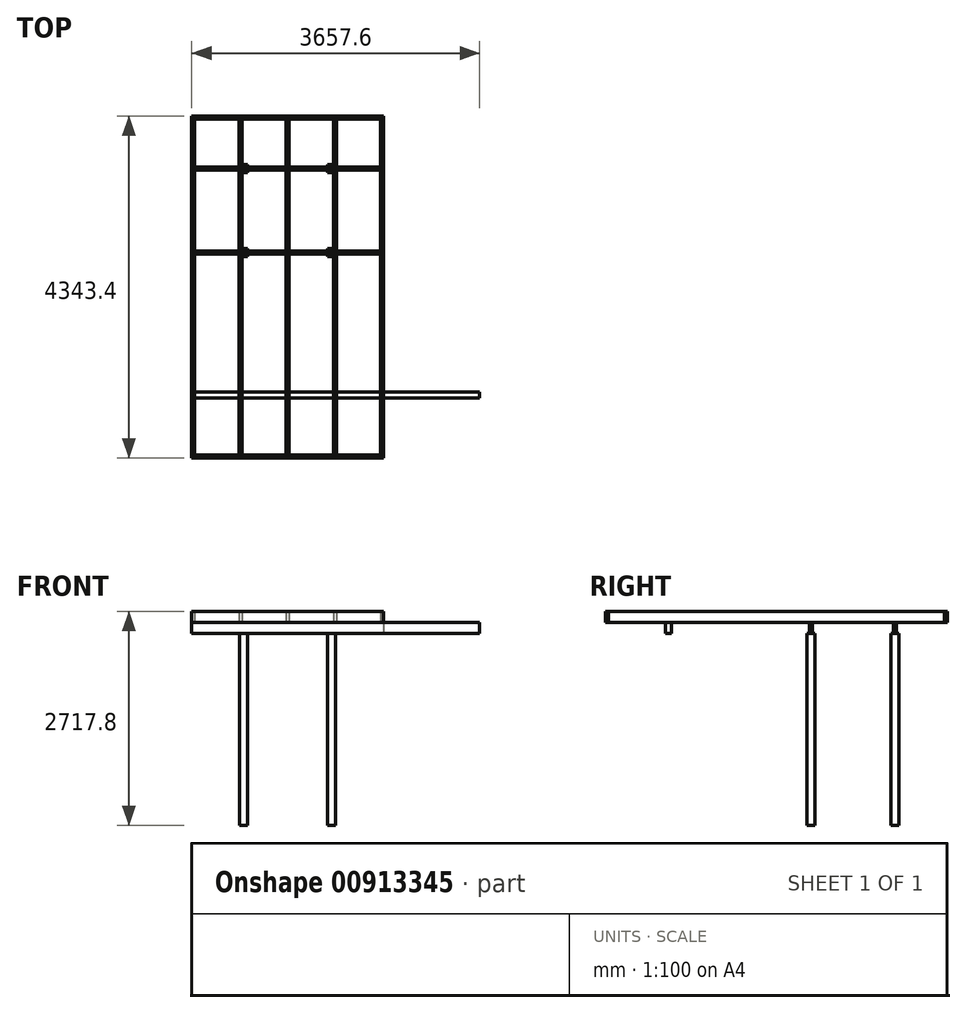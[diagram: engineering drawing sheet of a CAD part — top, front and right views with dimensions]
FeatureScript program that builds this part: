
annotation { "Feature Type Name" : "Feature", "Feature Type Description" : "" }
export const myFeature = defineFeature(function(context is Context, id is Id, definition is map)
    precondition{}
    {
        {
            var Q0;
            Q0=qCreatedBy(makeId("Top.planeOp"),FACE);
            var sketch = newSketch(context, id + "F0", { "sketchPlane" : qUnion([Q0])});
            skLineSegment(sketch, "E0.bottom", {"start": v(-738.08, 153.56) * mm, "end": v(-636.48, 153.56) * mm});
            skLineSegment(sketch, "E0.top", {"start": v(-738.08, 51.96) * mm, "end": v(-636.48, 51.96) * mm});
            skLineSegment(sketch, "E0.left", {"start": v(-738.08, 153.56) * mm, "end": v(-738.08, 51.96) * mm});
            skLineSegment(sketch, "E0.right", {"start": v(-636.48, 153.56) * mm, "end": v(-636.48, 51.96) * mm});
            skLineSegment(sketch, "E1.bottom", {"start": v(379.52, 153.56) * mm, "end": v(481.12, 153.56) * mm});
            skLineSegment(sketch, "E1.top", {"start": v(379.52, 51.96) * mm, "end": v(481.12, 51.96) * mm});
            skLineSegment(sketch, "E1.left", {"start": v(379.52, 153.56) * mm, "end": v(379.52, 51.96) * mm});
            skLineSegment(sketch, "E1.right", {"start": v(481.12, 153.56) * mm, "end": v(481.12, 51.96) * mm});
            skLineSegment(sketch, "E2.direction1", {"start": v(-738.08, 51.96) * mm, "end": v(-712.68, 51.96) * mm, "construction": true});
            skLineSegment(sketch, "E3.bottom", {"start": v(-1347.68, 83.71) * mm, "end": v(1090.72, 83.71) * mm});
            skLineSegment(sketch, "E3.top", {"start": v(-1347.68, 121.81) * mm, "end": v(1090.72, 121.81) * mm});
            skLineSegment(sketch, "E3.left", {"start": v(-1347.68, 83.71) * mm, "end": v(-1347.68, 121.81) * mm});
            skLineSegment(sketch, "E3.right", {"start": v(1090.72, 83.71) * mm, "end": v(1090.72, 121.81) * mm});
            skPoint(sketch, "E4", {"position": v(-738.08, 102.76) * mm});
            skPoint(sketch, "E5", {"position": v(-1347.68, 83.71) * mm});
            skPoint(sketch, "E6", {"position": v(-1347.68, 102.76) * mm});
            skLineSegment(sketch, "E7", {"start": v(-738.08, 102.76) * mm, "end": v(-852.86, 102.76) * mm});
            skLineSegment(sketch, "E8.0.1.0", {"start": v(481.12, -913.24) * mm, "end": v(481.12, -1014.84) * mm});
            skLineSegment(sketch, "E8.0.1.1", {"start": v(379.52, -913.24) * mm, "end": v(379.52, -1014.84) * mm});
            skLineSegment(sketch, "E8.0.1.2", {"start": v(-1347.68, -944.99) * mm, "end": v(1090.72, -944.99) * mm});
            skLineSegment(sketch, "E8.0.1.3", {"start": v(-738.08, -913.24) * mm, "end": v(-636.48, -913.24) * mm});
            skLineSegment(sketch, "E8.0.1.4", {"start": v(-636.48, -913.24) * mm, "end": v(-636.48, -1014.84) * mm});
            skPoint(sketch, "E8.0.1.5", {"position": v(-1347.68, -983.09) * mm});
            skPoint(sketch, "E8.0.1.6", {"position": v(-1347.68, -964.04) * mm});
            skLineSegment(sketch, "E8.0.1.7", {"start": v(379.52, -913.24) * mm, "end": v(481.12, -913.24) * mm});
            skPoint(sketch, "E8.0.1.8", {"position": v(-738.08, -964.04) * mm});
            skLineSegment(sketch, "E8.0.1.9", {"start": v(-738.08, -964.04) * mm, "end": v(-852.86, -964.04) * mm});
            skLineSegment(sketch, "E8.0.1.10", {"start": v(-1347.68, -983.09) * mm, "end": v(1090.72, -983.09) * mm});
            skLineSegment(sketch, "E8.0.1.11", {"start": v(379.52, -1014.84) * mm, "end": v(481.12, -1014.84) * mm});
            skLineSegment(sketch, "E8.0.1.12", {"start": v(-738.08, -1014.84) * mm, "end": v(-636.48, -1014.84) * mm});
            skLineSegment(sketch, "E8.0.1.13", {"start": v(1090.72, -983.09) * mm, "end": v(1090.72, -944.99) * mm});
            skLineSegment(sketch, "E8.0.1.14", {"start": v(-738.08, -913.24) * mm, "end": v(-738.08, -1014.84) * mm});
            skLineSegment(sketch, "E8.0.1.15", {"start": v(-1347.68, -983.09) * mm, "end": v(-1347.68, -944.99) * mm});
            skLineSegment(sketch, "E8.0.1.16", {"start": v(-738.08, -1014.84) * mm, "end": v(-712.68, -1014.84) * mm, "construction": true});
            skLineSegment(sketch, "E8.direction1", {"start": v(-1347.68, 83.71) * mm, "end": v(-1322.28, 83.71) * mm, "construction": true});
            skLineSegment(sketch, "E8.direction2", {"start": v(-1347.68, 83.71) * mm, "end": v(-1347.68, -983.09) * mm, "construction": true});
            skLineSegment(sketch, "E9.bottom", {"start": v(-1347.68, -2811.89) * mm, "end": v(2309.92, -2811.89) * mm});
            skLineSegment(sketch, "E9.top", {"start": v(-1347.68, -2735.69) * mm, "end": v(2309.92, -2735.69) * mm});
            skLineSegment(sketch, "E9.left", {"start": v(-1347.68, -2811.89) * mm, "end": v(-1347.68, -2735.69) * mm});
            skLineSegment(sketch, "E9.right", {"start": v(2309.92, -2811.89) * mm, "end": v(2309.92, -2735.69) * mm});
            skLineSegment(sketch, "E10.bottom", {"start": v(-1347.68, -3421.49) * mm, "end": v(-1309.58, -3421.49) * mm});
            skLineSegment(sketch, "E11.direction1", {"start": v(-1347.68, -3421.49) * mm, "end": v(-747.6, -3421.49) * mm, "construction": true});
            skLineSegment(sketch, "E12.left", {"start": v(-1347.68, -3421.49) * mm, "end": v(-1347.68, -3459.59) * mm});
            skLineSegment(sketch, "E12.right", {"start": v(1090.72, -3421.49) * mm, "end": v(1090.72, -3459.59) * mm});
            skSolve(sketch);
        }
        {
            var Q0;
            {var subQ0=sQuery(id+"F0.wireOp",EDGE,"E8.0.1.2");var subQ1=sQuery(id+"F0.wireOp",EDGE,"E8.0.1.0");var subQ2=makeQuery(id+"F0.imprint","INTERSECT",VERTEX,{"derivedFrom":[subQ1,subQ0]});Q0=makeQuery(id+"F0.imprint","IMPRINT",FACE,{"disambiguationData":[TD([[makeQuery(id+"F0.imprint","IMPRINT",EDGE,{"disambiguationData":[TD([[subQ2,-1.0]])],"derivedFrom":subQ1}),-1.0]])]});}
            var Q1;
            {var subQ0=sQuery(id+"F0.wireOp",EDGE,"E0.bottom");Q1=makeQuery(id+"F0.imprint","IMPRINT",FACE,{"disambiguationData":[TD([[makeQuery(id+"F0.imprint","IMPRINT",EDGE,{"derivedFrom":subQ0}),-1.0]])]});}
            var Q2;
            {var subQ5=sQuery(id+"F0.wireOp",EDGE,"E0.left");var subQ7=makeQuery(id+"F0.imprint","IMPRINT",VERTEX,{"derivedFrom":subQ5});Q2=makeQuery(id+"F0.imprint","IMPRINT",FACE,{"disambiguationData":[TD([[makeQuery(id+"F0.imprint","IMPRINT",EDGE,{"disambiguationData":[TD([[subQ7,1.0]])],"derivedFrom":subQ5}),1.0]])]});}
            var Q3;
            {var subQ0=sQuery(id+"F0.wireOp",EDGE,"E0.top");Q3=makeQuery(id+"F0.imprint","IMPRINT",FACE,{"disambiguationData":[TD([[makeQuery(id+"F0.imprint","IMPRINT",EDGE,{"derivedFrom":subQ0}),1.0]])]});}
            var Q4;
            {var subQ0=sQuery(id+"F0.wireOp",EDGE,"E1.bottom");Q4=makeQuery(id+"F0.imprint","IMPRINT",FACE,{"disambiguationData":[TD([[makeQuery(id+"F0.imprint","IMPRINT",EDGE,{"derivedFrom":subQ0}),-1.0]])]});}
            var Q5;
            {var subQ0=sQuery(id+"F0.wireOp",EDGE,"E3.top");var subQ1=sQuery(id+"F0.wireOp",EDGE,"E1.left");var subQ2=makeQuery(id+"F0.imprint","INTERSECT",VERTEX,{"derivedFrom":[subQ1,subQ0]});Q5=makeQuery(id+"F0.imprint","IMPRINT",FACE,{"disambiguationData":[TD([[makeQuery(id+"F0.imprint","IMPRINT",EDGE,{"disambiguationData":[TD([[subQ2,-1.0]])],"derivedFrom":subQ1}),1.0]])]});}
            var Q6;
            {var subQ0=sQuery(id+"F0.wireOp",EDGE,"E1.top");Q6=makeQuery(id+"F0.imprint","IMPRINT",FACE,{"disambiguationData":[TD([[makeQuery(id+"F0.imprint","IMPRINT",EDGE,{"derivedFrom":subQ0}),1.0]])]});}
            var Q7;
            {var subQ0=sQuery(id+"F0.wireOp",EDGE,"E8.0.1.12");Q7=makeQuery(id+"F0.imprint","IMPRINT",FACE,{"disambiguationData":[TD([[makeQuery(id+"F0.imprint","IMPRINT",EDGE,{"derivedFrom":subQ0}),1.0]])]});}
            var Q8;
            {var subQ0=sQuery(id+"F0.wireOp",EDGE,"E8.0.1.7");Q8=makeQuery(id+"F0.imprint","IMPRINT",FACE,{"disambiguationData":[TD([[makeQuery(id+"F0.imprint","IMPRINT",EDGE,{"derivedFrom":subQ0}),-1.0]])]});}
            var Q9;
            {var subQ5=sQuery(id+"F0.wireOp",EDGE,"E8.0.1.3");Q9=makeQuery(id+"F0.imprint","IMPRINT",FACE,{"disambiguationData":[TD([[makeQuery(id+"F0.imprint","IMPRINT",EDGE,{"derivedFrom":subQ5}),-1.0]])]});}
            var Q10;
            {var subQ0=sQuery(id+"F0.wireOp",EDGE,"E8.0.1.11");Q10=makeQuery(id+"F0.imprint","IMPRINT",FACE,{"disambiguationData":[TD([[makeQuery(id+"F0.imprint","IMPRINT",EDGE,{"derivedFrom":subQ0}),1.0]])]});}
            var Q11;
            {var subQ0=sQuery(id+"F0.wireOp",EDGE,"E8.0.1.14");var subQ1=makeQuery(id+"F0.imprint","IMPRINT",VERTEX,{"derivedFrom":subQ0});Q11=makeQuery(id+"F0.imprint","IMPRINT",FACE,{"disambiguationData":[TD([[makeQuery(id+"F0.imprint","IMPRINT",EDGE,{"disambiguationData":[TD([[subQ1,1.0]])],"derivedFrom":subQ0}),1.0]])]});}
            extrude(context, id + "F1", {"entities" : qUnion([Q0, Q1, Q2, Q3, Q4, Q5, Q6, Q7, Q8, Q9, Q10, Q11]), "oppositeDirection" : true, "depth" : 2438.4 * mm, "offsetDistance" : 25.4 * mm});
        }
        {
            var Q0;
            {var subQ0=sQuery(id+"F0.wireOp",EDGE,"E3.left");Q0=makeQuery(id+"F0.imprint","IMPRINT",FACE,{"disambiguationData":[TD([[makeQuery(id+"F0.imprint","IMPRINT",EDGE,{"derivedFrom":subQ0}),-1.0]])]});}
            var Q1;
            {var subQ5=sQuery(id+"F0.wireOp",EDGE,"E0.left");var subQ7=makeQuery(id+"F0.imprint","IMPRINT",VERTEX,{"derivedFrom":subQ5});Q1=makeQuery(id+"F0.imprint","IMPRINT",FACE,{"disambiguationData":[TD([[makeQuery(id+"F0.imprint","IMPRINT",EDGE,{"disambiguationData":[TD([[subQ7,1.0]])],"derivedFrom":subQ5}),1.0]])]});}
            var Q2;
            {var subQ0=sQuery(id+"F0.wireOp",EDGE,"E3.top");var subQ1=sQuery(id+"F0.wireOp",EDGE,"E0.right");var subQ2=makeQuery(id+"F0.imprint","INTERSECT",VERTEX,{"derivedFrom":[subQ1,subQ0]});Q2=makeQuery(id+"F0.imprint","IMPRINT",FACE,{"disambiguationData":[TD([[makeQuery(id+"F0.imprint","IMPRINT",EDGE,{"disambiguationData":[TD([[subQ2,-1.0]])],"derivedFrom":subQ1}),1.0]])]});}
            var Q3;
            {var subQ0=sQuery(id+"F0.wireOp",EDGE,"E3.top");var subQ1=sQuery(id+"F0.wireOp",EDGE,"E1.left");var subQ2=makeQuery(id+"F0.imprint","INTERSECT",VERTEX,{"derivedFrom":[subQ1,subQ0]});Q3=makeQuery(id+"F0.imprint","IMPRINT",FACE,{"disambiguationData":[TD([[makeQuery(id+"F0.imprint","IMPRINT",EDGE,{"disambiguationData":[TD([[subQ2,-1.0]])],"derivedFrom":subQ1}),1.0]])]});}
            var Q4;
            {var subQ5=sQuery(id+"F0.wireOp",EDGE,"E3.right");Q4=makeQuery(id+"F0.imprint","IMPRINT",FACE,{"disambiguationData":[TD([[makeQuery(id+"F0.imprint","IMPRINT",EDGE,{"derivedFrom":subQ5}),1.0]])]});}
            var Q5;
            {var subQ6=sQuery(id+"F0.wireOp",EDGE,"E8.0.1.15");Q5=makeQuery(id+"F0.imprint","IMPRINT",FACE,{"disambiguationData":[TD([[makeQuery(id+"F0.imprint","IMPRINT",EDGE,{"derivedFrom":subQ6}),-1.0]])]});}
            var Q6;
            {var subQ0=sQuery(id+"F0.wireOp",EDGE,"E8.0.1.14");var subQ1=makeQuery(id+"F0.imprint","IMPRINT",VERTEX,{"derivedFrom":subQ0});Q6=makeQuery(id+"F0.imprint","IMPRINT",FACE,{"disambiguationData":[TD([[makeQuery(id+"F0.imprint","IMPRINT",EDGE,{"disambiguationData":[TD([[subQ1,1.0]])],"derivedFrom":subQ0}),1.0]])]});}
            var Q7;
            {var subQ0=sQuery(id+"F0.wireOp",EDGE,"E8.0.1.2");var subQ1=sQuery(id+"F0.wireOp",EDGE,"E8.0.1.1");var subQ2=makeQuery(id+"F0.imprint","INTERSECT",VERTEX,{"derivedFrom":[subQ1,subQ0]});Q7=makeQuery(id+"F0.imprint","IMPRINT",FACE,{"disambiguationData":[TD([[makeQuery(id+"F0.imprint","IMPRINT",EDGE,{"disambiguationData":[TD([[subQ2,-1.0]])],"derivedFrom":subQ1}),-1.0]])]});}
            var Q8;
            {var subQ0=sQuery(id+"F0.wireOp",EDGE,"E8.0.1.2");var subQ1=sQuery(id+"F0.wireOp",EDGE,"E8.0.1.0");var subQ2=makeQuery(id+"F0.imprint","INTERSECT",VERTEX,{"derivedFrom":[subQ1,subQ0]});Q8=makeQuery(id+"F0.imprint","IMPRINT",FACE,{"disambiguationData":[TD([[makeQuery(id+"F0.imprint","IMPRINT",EDGE,{"disambiguationData":[TD([[subQ2,-1.0]])],"derivedFrom":subQ1}),-1.0]])]});}
            var Q9;
            {var subQ5=sQuery(id+"F0.wireOp",EDGE,"E8.0.1.13");Q9=makeQuery(id+"F0.imprint","IMPRINT",FACE,{"disambiguationData":[TD([[makeQuery(id+"F0.imprint","IMPRINT",EDGE,{"derivedFrom":subQ5}),1.0]])]});}
            var Q10;
            Q10=makeQuery(id+"F0.imprint","IMPRINT",FACE,{"disambiguationData":[TD([[makeQuery(id+"F0.imprint","IMPRINT",EDGE,{"derivedFrom":sQuery(id+"F0.wireOp",EDGE,"E9.bottom")}),1.0]])]});
            extrude(context, id + "F2", {"entities" : qUnion([Q0, Q1, Q2, Q3, Q4, Q5, Q6, Q7, Q8, Q9, Q10]), "depth" : 139.7 * mm, "offsetDistance" : 25.4 * mm});
        }
        {
            var Q0;
            Q0=makeQuery(id+"F2.opExtrude","CAP_FACE",FACE,{"disambiguationData":[OSD([sQuery(id+"F0.wireOp",EDGE,"E0.bottom"),sQuery(id+"F0.wireOp",EDGE,"E0.top"),sQuery(id+"F0.wireOp",EDGE,"E0.left"),sQuery(id+"F0.wireOp",EDGE,"E0.right"),sQuery(id+"F0.wireOp",EDGE,"E3.bottom"),sQuery(id+"F0.wireOp",EDGE,"E3.top"),sQuery(id+"F0.wireOp",EDGE,"E3.left"),sQuery(id+"F0.wireOp",EDGE,"E3.right")])],"isStart":false});
            var sketch = newSketch(context, id + "F3", { "sketchPlane" : qUnion([Q0])});
            skLineSegment(sketch, "E13.bottom", {"start": v(-1347.68, 731.41) * mm, "end": v(-1309.58, 731.41) * mm});
            skLineSegment(sketch, "E13.top", {"start": v(-1347.68, -3535.79) * mm, "end": v(-1309.58, -3535.79) * mm});
            skLineSegment(sketch, "E13.left", {"start": v(-1347.68, 731.41) * mm, "end": v(-1347.68, -3535.79) * mm});
            skLineSegment(sketch, "E13.right", {"start": v(-1309.58, 731.41) * mm, "end": v(-1309.58, -3535.79) * mm});
            skLineSegment(sketch, "E14.1.0.0", {"start": v(-709.5, 731.41) * mm, "end": v(-709.5, -3535.79) * mm});
            skLineSegment(sketch, "E14.1.0.1", {"start": v(-747.6, 731.41) * mm, "end": v(-747.6, -3535.79) * mm});
            skLineSegment(sketch, "E14.1.0.2", {"start": v(-747.6, -3535.79) * mm, "end": v(-709.5, -3535.79) * mm});
            skLineSegment(sketch, "E14.1.0.3", {"start": v(-747.6, 731.41) * mm, "end": v(-709.5, 731.41) * mm});
            skLineSegment(sketch, "E14.2.0.0", {"start": v(-109.43, 731.41) * mm, "end": v(-109.43, -3535.79) * mm});
            skLineSegment(sketch, "E14.2.0.1", {"start": v(-147.53, 731.41) * mm, "end": v(-147.53, -3535.79) * mm});
            skLineSegment(sketch, "E14.2.0.2", {"start": v(-147.53, -3535.79) * mm, "end": v(-109.43, -3535.79) * mm});
            skLineSegment(sketch, "E14.2.0.3", {"start": v(-147.53, 731.41) * mm, "end": v(-109.43, 731.41) * mm});
            skLineSegment(sketch, "E14.3.0.0", {"start": v(490.64, 731.41) * mm, "end": v(490.64, -3535.79) * mm});
            skLineSegment(sketch, "E14.3.0.1", {"start": v(452.54, 731.41) * mm, "end": v(452.54, -3535.79) * mm});
            skLineSegment(sketch, "E14.3.0.2", {"start": v(452.54, -3535.79) * mm, "end": v(490.64, -3535.79) * mm});
            skLineSegment(sketch, "E14.3.0.3", {"start": v(452.54, 731.41) * mm, "end": v(490.64, 731.41) * mm});
            skLineSegment(sketch, "E14.4.0.0", {"start": v(1090.72, 731.41) * mm, "end": v(1090.72, -3535.79) * mm});
            skLineSegment(sketch, "E14.4.0.1", {"start": v(1052.62, 731.41) * mm, "end": v(1052.62, -3535.79) * mm});
            skLineSegment(sketch, "E14.4.0.2", {"start": v(1052.62, -3535.79) * mm, "end": v(1090.72, -3535.79) * mm});
            skLineSegment(sketch, "E14.4.0.3", {"start": v(1052.62, 731.41) * mm, "end": v(1090.72, 731.41) * mm});
            skLineSegment(sketch, "E14.direction1", {"start": v(-1347.68, -3535.79) * mm, "end": v(-747.6, -3535.79) * mm, "construction": true});
            skLineSegment(sketch, "E15.bottom", {"start": v(-1347.68, 731.41) * mm, "end": v(1090.72, 731.41) * mm});
            skLineSegment(sketch, "E15.top", {"start": v(-1347.68, 769.51) * mm, "end": v(1090.72, 769.51) * mm});
            skLineSegment(sketch, "E15.left", {"start": v(-1347.68, 731.41) * mm, "end": v(-1347.68, 769.51) * mm});
            skLineSegment(sketch, "E15.right", {"start": v(1090.72, 731.41) * mm, "end": v(1090.72, 769.51) * mm});
            skLineSegment(sketch, "E16.bottom", {"start": v(-1347.68, -3535.79) * mm, "end": v(1090.72, -3535.79) * mm});
            skLineSegment(sketch, "E16.top", {"start": v(-1347.68, -3573.89) * mm, "end": v(1090.72, -3573.89) * mm});
            skLineSegment(sketch, "E16.left", {"start": v(-1347.68, -3535.79) * mm, "end": v(-1347.68, -3573.89) * mm});
            skLineSegment(sketch, "E16.right", {"start": v(1090.72, -3535.79) * mm, "end": v(1090.72, -3573.89) * mm});
            skSolve(sketch);
        }
        {
            var Q0;
            Q0=makeQuery(id+"F3.imprint","IMPRINT",FACE,{"disambiguationData":[TD([[makeQuery(id+"F3.imprint","IMPRINT",EDGE,{"derivedFrom":sQuery(id+"F3.wireOp",EDGE,"E15.top")}),-1.0]])]});
            var Q1;
            Q1=makeQuery(id+"F3.imprint","IMPRINT",FACE,{"disambiguationData":[TD([[makeQuery(id+"F3.imprint","IMPRINT",EDGE,{"derivedFrom":sQuery(id+"F3.wireOp",EDGE,"E16.top")}),1.0]])]});
            extrude(context, id + "F4", {"entities" : qUnion([Q0, Q1]), "depth" : 139.7 * mm, "offsetDistance" : 25.4 * mm});
        }
        {
            var Q0;
            {var subQ3=sQuery(id+"F3.wireOp",EDGE,"E16.bottom");var subQ5=sQuery(id+"F3.wireOp",EDGE,"E13.right");var subQ6=makeQuery(id+"F3.imprint","INTERSECT",VERTEX,{"derivedFrom":[subQ5,subQ3]});Q0=makeQuery(id+"F3.imprint","IMPRINT",FACE,{"disambiguationData":[TD([[makeQuery(id+"F3.imprint","IMPRINT",EDGE,{"disambiguationData":[TD([[subQ6,1.0]])],"derivedFrom":subQ5}),-1.0]])]});}
            var Q1;
            {var subQ0=sQuery(id+"F3.wireOp",EDGE,"E16.bottom");var subQ1=sQuery(id+"F3.wireOp",EDGE,"E14.1.0.0");var subQ2=makeQuery(id+"F3.imprint","INTERSECT",VERTEX,{"derivedFrom":[subQ1,subQ0]});Q1=makeQuery(id+"F3.imprint","IMPRINT",FACE,{"disambiguationData":[TD([[makeQuery(id+"F3.imprint","IMPRINT",EDGE,{"disambiguationData":[TD([[subQ2,1.0]])],"derivedFrom":subQ1}),-1.0]])]});}
            var Q2;
            {var subQ0=sQuery(id+"F3.wireOp",EDGE,"E16.bottom");var subQ1=sQuery(id+"F3.wireOp",EDGE,"E14.2.0.0");var subQ2=makeQuery(id+"F3.imprint","INTERSECT",VERTEX,{"derivedFrom":[subQ1,subQ0]});Q2=makeQuery(id+"F3.imprint","IMPRINT",FACE,{"disambiguationData":[TD([[makeQuery(id+"F3.imprint","IMPRINT",EDGE,{"disambiguationData":[TD([[subQ2,1.0]])],"derivedFrom":subQ1}),-1.0]])]});}
            var Q3;
            {var subQ0=sQuery(id+"F3.wireOp",EDGE,"E16.bottom");var subQ1=sQuery(id+"F3.wireOp",EDGE,"E14.3.0.0");var subQ2=makeQuery(id+"F3.imprint","INTERSECT",VERTEX,{"derivedFrom":[subQ1,subQ0]});Q3=makeQuery(id+"F3.imprint","IMPRINT",FACE,{"disambiguationData":[TD([[makeQuery(id+"F3.imprint","IMPRINT",EDGE,{"disambiguationData":[TD([[subQ2,1.0]])],"derivedFrom":subQ1}),-1.0]])]});}
            var Q4;
            {var subQ3=sQuery(id+"F3.wireOp",EDGE,"E16.bottom");var subQ5=sQuery(id+"F3.wireOp",EDGE,"E14.4.0.1");var subQ6=makeQuery(id+"F3.imprint","INTERSECT",VERTEX,{"derivedFrom":[subQ5,subQ3]});Q4=makeQuery(id+"F3.imprint","IMPRINT",FACE,{"disambiguationData":[TD([[makeQuery(id+"F3.imprint","IMPRINT",EDGE,{"disambiguationData":[TD([[subQ6,1.0]])],"derivedFrom":subQ5}),1.0]])]});}
            var Q5;
            {var subQ0=sQuery(id+"F3.wireOp",EDGE,"E13.left");var subQ1=makeQuery(id+"F2.opExtrude","CAP_EDGE",EDGE,{"disambiguationData":[OSD([sQuery(id+"F0.wireOp",EDGE,"E3.bottom")])],"isStart":false});var subQ2=makeQuery(id+"F3.imprint","INTERSECT",VERTEX,{"derivedFrom":[subQ1,subQ0]});var subQ3=makeQuery(id+"F2.opExtrude","CAP_EDGE",EDGE,{"disambiguationData":[OSD([sQuery(id+"F0.wireOp",EDGE,"E3.top")])],"isStart":false});var subQ4=makeQuery(id+"F3.imprint","INTERSECT",VERTEX,{"derivedFrom":[subQ3,subQ0]});Q5=makeQuery(id+"F3.imprint","IMPRINT",FACE,{"disambiguationData":[TD([[makeQuery(id+"F3.imprint","IMPRINT",EDGE,{"disambiguationData":[TD([[subQ2,-1.0],[subQ4,1.0]])],"derivedFrom":subQ0}),-1.0]])]});}
            var Q6;
            {var subQ3=sQuery(id+"F3.wireOp",EDGE,"E15.bottom");var subQ5=sQuery(id+"F3.wireOp",EDGE,"E13.right");var subQ6=makeQuery(id+"F3.imprint","INTERSECT",VERTEX,{"derivedFrom":[subQ5,subQ3]});Q6=makeQuery(id+"F3.imprint","IMPRINT",FACE,{"disambiguationData":[TD([[makeQuery(id+"F3.imprint","IMPRINT",EDGE,{"disambiguationData":[TD([[subQ6,-1.0]])],"derivedFrom":subQ5}),-1.0]])]});}
            var Q7;
            {var subQ0=sQuery(id+"F3.wireOp",EDGE,"E15.bottom");var subQ1=sQuery(id+"F3.wireOp",EDGE,"E14.1.0.0");var subQ2=makeQuery(id+"F3.imprint","INTERSECT",VERTEX,{"derivedFrom":[subQ1,subQ0]});Q7=makeQuery(id+"F3.imprint","IMPRINT",FACE,{"disambiguationData":[TD([[makeQuery(id+"F3.imprint","IMPRINT",EDGE,{"disambiguationData":[TD([[subQ2,-1.0]])],"derivedFrom":subQ1}),-1.0]])]});}
            var Q8;
            {var subQ0=sQuery(id+"F3.wireOp",EDGE,"E14.1.0.0");var subQ1=makeQuery(id+"F2.opExtrude","CAP_EDGE",EDGE,{"disambiguationData":[OSD([sQuery(id+"F0.wireOp",EDGE,"E3.top")])],"isStart":false});var subQ2=makeQuery(id+"F3.imprint","INTERSECT",VERTEX,{"derivedFrom":[subQ1,subQ0]});Q8=makeQuery(id+"F3.imprint","IMPRINT",FACE,{"disambiguationData":[TD([[makeQuery(id+"F3.imprint","IMPRINT",EDGE,{"disambiguationData":[TD([[subQ2,-1.0]])],"derivedFrom":subQ0}),-1.0]])]});}
            var Q9;
            {var subQ0=sQuery(id+"F3.wireOp",EDGE,"E14.2.0.0");var subQ1=makeQuery(id+"F2.opExtrude","CAP_EDGE",EDGE,{"disambiguationData":[OSD([sQuery(id+"F0.wireOp",EDGE,"E3.top")])],"isStart":false});var subQ2=makeQuery(id+"F3.imprint","INTERSECT",VERTEX,{"derivedFrom":[subQ1,subQ0]});Q9=makeQuery(id+"F3.imprint","IMPRINT",FACE,{"disambiguationData":[TD([[makeQuery(id+"F3.imprint","IMPRINT",EDGE,{"disambiguationData":[TD([[subQ2,-1.0]])],"derivedFrom":subQ0}),-1.0]])]});}
            var Q10;
            {var subQ0=sQuery(id+"F3.wireOp",EDGE,"E15.bottom");var subQ1=sQuery(id+"F3.wireOp",EDGE,"E14.2.0.0");var subQ2=makeQuery(id+"F3.imprint","INTERSECT",VERTEX,{"derivedFrom":[subQ1,subQ0]});Q10=makeQuery(id+"F3.imprint","IMPRINT",FACE,{"disambiguationData":[TD([[makeQuery(id+"F3.imprint","IMPRINT",EDGE,{"disambiguationData":[TD([[subQ2,-1.0]])],"derivedFrom":subQ1}),-1.0]])]});}
            var Q11;
            {var subQ0=sQuery(id+"F3.wireOp",EDGE,"E15.bottom");var subQ1=sQuery(id+"F3.wireOp",EDGE,"E14.3.0.0");var subQ2=makeQuery(id+"F3.imprint","INTERSECT",VERTEX,{"derivedFrom":[subQ1,subQ0]});Q11=makeQuery(id+"F3.imprint","IMPRINT",FACE,{"disambiguationData":[TD([[makeQuery(id+"F3.imprint","IMPRINT",EDGE,{"disambiguationData":[TD([[subQ2,-1.0]])],"derivedFrom":subQ1}),-1.0]])]});}
            var Q12;
            {var subQ3=sQuery(id+"F3.wireOp",EDGE,"E15.bottom");var subQ5=sQuery(id+"F3.wireOp",EDGE,"E14.4.0.1");var subQ6=makeQuery(id+"F3.imprint","INTERSECT",VERTEX,{"derivedFrom":[subQ5,subQ3]});Q12=makeQuery(id+"F3.imprint","IMPRINT",FACE,{"disambiguationData":[TD([[makeQuery(id+"F3.imprint","IMPRINT",EDGE,{"disambiguationData":[TD([[subQ6,-1.0]])],"derivedFrom":subQ5}),1.0]])]});}
            var Q13;
            {var subQ0=sQuery(id+"F3.wireOp",EDGE,"E14.4.0.0");var subQ1=makeQuery(id+"F2.opExtrude","CAP_EDGE",EDGE,{"disambiguationData":[OSD([sQuery(id+"F0.wireOp",EDGE,"E3.bottom")])],"isStart":false});var subQ2=makeQuery(id+"F3.imprint","INTERSECT",VERTEX,{"derivedFrom":[subQ1,subQ0]});var subQ3=makeQuery(id+"F2.opExtrude","CAP_EDGE",EDGE,{"disambiguationData":[OSD([sQuery(id+"F0.wireOp",EDGE,"E3.top")])],"isStart":false});var subQ4=makeQuery(id+"F3.imprint","INTERSECT",VERTEX,{"derivedFrom":[subQ3,subQ0]});Q13=makeQuery(id+"F3.imprint","IMPRINT",FACE,{"disambiguationData":[TD([[makeQuery(id+"F3.imprint","IMPRINT",EDGE,{"disambiguationData":[TD([[subQ2,-1.0],[subQ4,1.0]])],"derivedFrom":subQ0}),1.0]])]});}
            var Q14;
            {var subQ0=sQuery(id+"F3.wireOp",EDGE,"E14.3.0.0");var subQ1=makeQuery(id+"F2.opExtrude","CAP_EDGE",EDGE,{"disambiguationData":[OSD([sQuery(id+"F0.wireOp",EDGE,"E3.top")])],"isStart":false});var subQ2=makeQuery(id+"F3.imprint","INTERSECT",VERTEX,{"derivedFrom":[subQ1,subQ0]});Q14=makeQuery(id+"F3.imprint","IMPRINT",FACE,{"disambiguationData":[TD([[makeQuery(id+"F3.imprint","IMPRINT",EDGE,{"disambiguationData":[TD([[subQ2,-1.0]])],"derivedFrom":subQ0}),-1.0]])]});}
            extrude(context, id + "F5", {"entities" : qUnion([Q0, Q1, Q2, Q3, Q4, Q5, Q6, Q7, Q8, Q9, Q10, Q11, Q12, Q13, Q14]), "depth" : 139.7 * mm, "offsetDistance" : 25.4 * mm});
        }
    });
